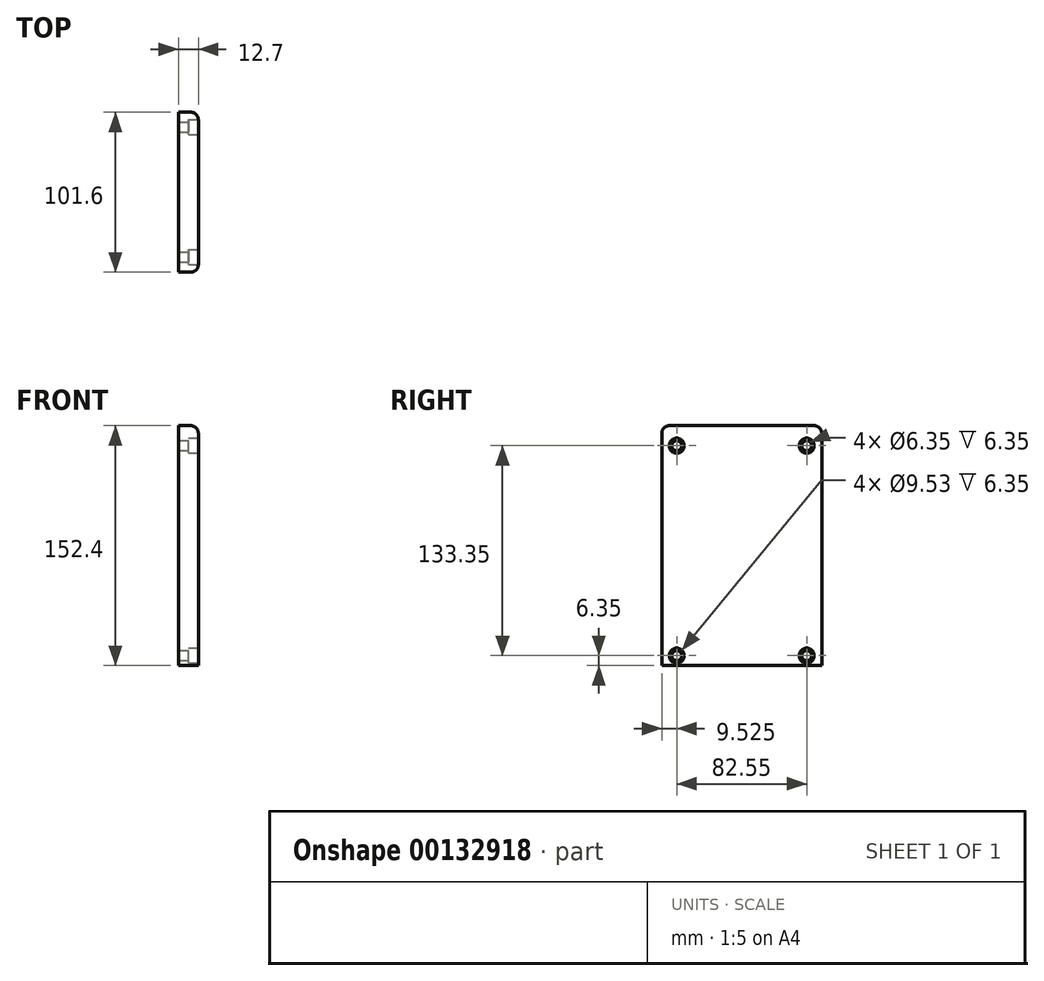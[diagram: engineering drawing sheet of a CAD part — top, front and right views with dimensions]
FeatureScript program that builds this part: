
annotation { "Feature Type Name" : "Feature", "Feature Type Description" : "" }
export const myFeature = defineFeature(function(context is Context, id is Id, definition is map)
    precondition{}
    {
        {
            var Q0;
            Q0=qCreatedBy(makeId("Right.planeOp"),FACE);
            var sketch = newSketch(context, id + "F0", { "sketchPlane" : qUnion([Q0])});
            skLineSegment(sketch, "E0.bottom", {"start": v(50.8, 76.2) * mm, "end": v(-50.8, 76.2) * mm});
            skLineSegment(sketch, "E0.top", {"start": v(50.8, -76.2) * mm, "end": v(-50.8, -76.2) * mm});
            skLineSegment(sketch, "E0.left", {"start": v(50.8, 76.2) * mm, "end": v(50.8, -76.2) * mm});
            skLineSegment(sketch, "E0.right", {"start": v(-50.8, 76.2) * mm, "end": v(-50.8, -76.2) * mm});
            skPoint(sketch, "E0.middle", {"position": v(0, 0) * mm});
            skPoint(sketch, "E1", {"position": v(-41.28, -69.85) * mm});
            skPoint(sketch, "E2.MirrorP", {"position": v(41.28, -69.85) * mm});
            skPoint(sketch, "E3", {"position": v(-41.28, 63.5) * mm});
            skPoint(sketch, "E4", {"position": v(41.28, 63.5) * mm});
            skSolve(sketch);
        }
        {
            var Q0;
            Q0=makeQuery(id+"F0.imprint","IMPRINT",FACE,{"disambiguationData":[TD([[makeQuery(id+"F0.imprint","IMPRINT",EDGE,{"derivedFrom":sQuery(id+"F0.wireOp",EDGE,"E0.bottom")}),1.0]])]});
            extrude(context, id + "F1", {"entities" : qUnion([Q0]), "oppositeDirection" : true, "depth" : 12.7 * mm});
        }
        {
            var Q0;
            Q0=sQuery(id+"F0.wireOp",VERTEX,"E1");
            var Q1;
            Q1=sQuery(id+"F0.wireOp",VERTEX,"E2.MirrorP");
            var Q2;
            Q2=sQuery(id+"F0.wireOp",VERTEX,"E3");
            var Q3;
            Q3=sQuery(id+"F0.wireOp",VERTEX,"E4");
            var Q4;
            Q4=makeQuery(id+"F1.opExtrude","SWEPT_BODY",BODY,{"disambiguationData":[OSD([sQuery(id+"F0.wireOp",EDGE,"E0.bottom"),sQuery(id+"F0.wireOp",EDGE,"E0.top"),sQuery(id+"F0.wireOp",EDGE,"E0.left"),sQuery(id+"F0.wireOp",EDGE,"E0.right")])]});
            hole(context, id + "F2", {"style" : HoleStyle.C_BORE, "endStyle" : HoleEndStyle.THROUGH, "holeDiameter" : 6.35 * mm, "cBoreDiameter" : 9.52 * mm, "cBoreDepth" : 6.35 * mm, "locations" : qUnion([Q0, Q1, Q2, Q3]), "scope" : qUnion([Q4]), "isTappedThrough" : true});
        }
        {
            var Q0;
            Q0=makeQuery(id+"F1.opExtrude","CAP_EDGE",EDGE,{"disambiguationData":[OSD([sQuery(id+"F0.wireOp",EDGE,"E0.bottom")])],"isStart":true});
            var Q1;
            Q1=makeQuery(id+"F1.opExtrude","CAP_EDGE",EDGE,{"disambiguationData":[OSD([sQuery(id+"F0.wireOp",EDGE,"E0.right")])],"isStart":true});
            var Q2;
            Q2=makeQuery(id+"F1.opExtrude","CAP_EDGE",EDGE,{"disambiguationData":[OSD([sQuery(id+"F0.wireOp",EDGE,"E0.left")])],"isStart":true});
            var Q3;
            Q3=makeQuery(id+"F1.opExtrude","SWEPT_EDGE",EDGE,{"disambiguationData":[OSD([sQuery(id+"F0.wireOp",EDGE,"E0.bottom"),sQuery(id+"F0.wireOp",EDGE,"E0.right")])]});
            var Q4;
            Q4=makeQuery(id+"F1.opExtrude","SWEPT_EDGE",EDGE,{"disambiguationData":[OSD([sQuery(id+"F0.wireOp",EDGE,"E0.bottom"),sQuery(id+"F0.wireOp",EDGE,"E0.left")])]});
            fillet(context, id + "F3", {"entities" : qUnion([Q0, Q1, Q2, Q3, Q4]), "radius" : 4.75 * mm, "tangentPropagation" : true, "allowEdgeOverflow" : false});
        }
    });
